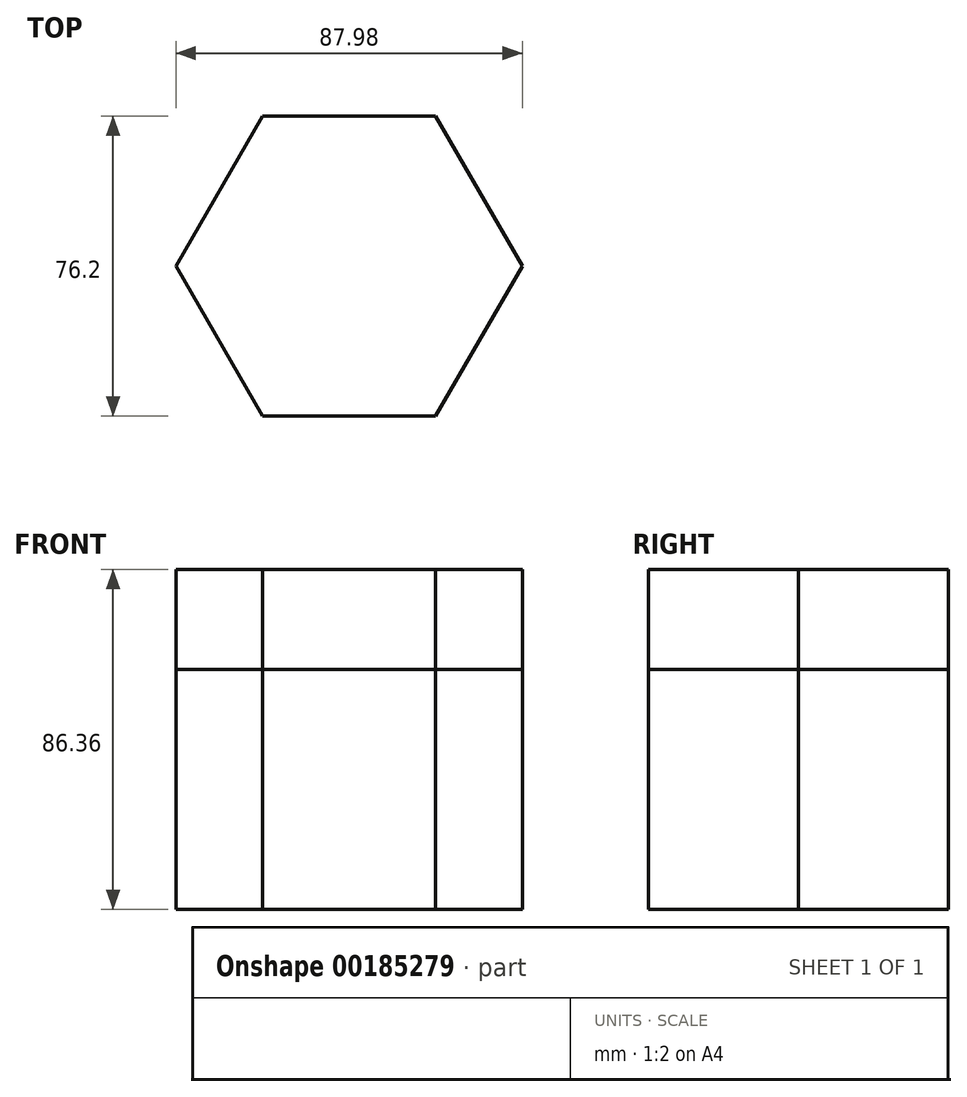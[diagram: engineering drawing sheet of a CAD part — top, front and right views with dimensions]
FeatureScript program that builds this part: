
annotation { "Feature Type Name" : "Feature", "Feature Type Description" : "" }
export const myFeature = defineFeature(function(context is Context, id is Id, definition is map)
    precondition{}
    {
        {
            var Q0;
            Q0=qCreatedBy(makeId("Top.planeOp"),FACE);
            var sketch = newSketch(context, id + "F0", { "sketchPlane" : qUnion([Q0])});
            skCircle(sketch, "E0.cCircle", {"center": v(0, 0) * mm, "radius": 38.1 * mm, "construction": true});
            skLineSegment(sketch, "E0.0", {"start": v(-22, 38.1) * mm, "end": v(22, 38.1) * mm});
            skLineSegment(sketch, "E0.1", {"start": v(22, 38.1) * mm, "end": v(44, 0) * mm});
            skLineSegment(sketch, "E0.2", {"start": v(44, 0) * mm, "end": v(22, -38.1) * mm});
            skLineSegment(sketch, "E0.3", {"start": v(22, -38.1) * mm, "end": v(-22, -38.1) * mm});
            skLineSegment(sketch, "E0.4", {"start": v(-22, -38.1) * mm, "end": v(-44, 0) * mm});
            skLineSegment(sketch, "E0.5", {"start": v(-44, 0) * mm, "end": v(-22, 38.1) * mm});
            skPoint(sketch, "E0.0.midPoint", {"position": v(0, 38.1) * mm});
            skSolve(sketch);
        }
        {
            var Q0;
            Q0 = qSketchRegion(id + "F0", true);
            extrude(context, id + "F1", {"entities" : qUnion([Q0]), "depth" : 60.96 * mm});
        }
        {
            var Q0;
            Q0=makeQuery(id+"F1.opExtrude","CAP_FACE",FACE,{"disambiguationData":[OSD([sQuery(id+"F0.wireOp",EDGE,"E0.0"),sQuery(id+"F0.wireOp",EDGE,"E0.1"),sQuery(id+"F0.wireOp",EDGE,"E0.2"),sQuery(id+"F0.wireOp",EDGE,"E0.3"),sQuery(id+"F0.wireOp",EDGE,"E0.4"),sQuery(id+"F0.wireOp",EDGE,"E0.5")])],"isStart":false});
            extrude(context, id + "F2", {"entities" : qUnion([Q0]), "depth" : 25.4 * mm});
        }
    });
